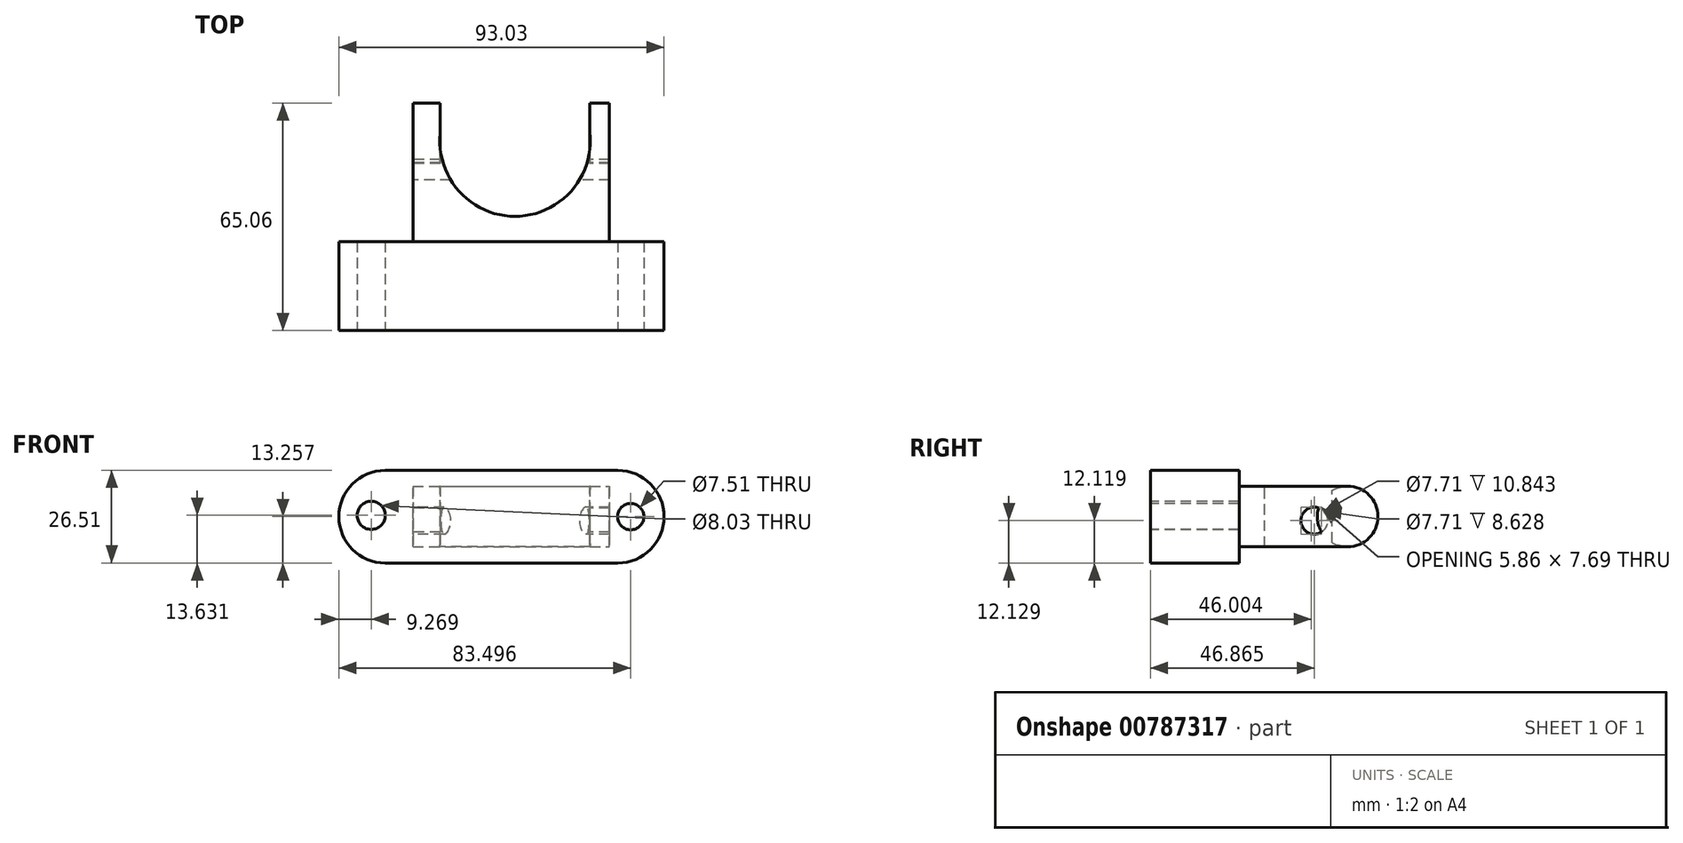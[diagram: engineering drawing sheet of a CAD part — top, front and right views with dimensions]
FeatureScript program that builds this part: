
annotation { "Feature Type Name" : "Feature", "Feature Type Description" : "" }
export const myFeature = defineFeature(function(context is Context, id is Id, definition is map)
    precondition{}
    {
        {
            var Q0;
            Q0=qCreatedBy(makeId("Front.planeOp"),FACE);
            var sketch = newSketch(context, id + "F0", { "sketchPlane" : qUnion([Q0])});
            skLineSegment(sketch, "E0.bottom", {"start": v(22.53, 17.47) * mm, "end": v(-43.98, 17.47) * mm});
            skLineSegment(sketch, "E0.top", {"start": v(22.53, -9.04) * mm, "end": v(-43.98, -9.04) * mm});
            skLineSegment(sketch, "E0.left", {"start": v(22.53, 17.47) * mm, "end": v(22.53, -9.04) * mm});
            skLineSegment(sketch, "E0.right", {"start": v(-43.98, 17.47) * mm, "end": v(-43.98, -9.04) * mm});
            skArc(sketch, "E1", {"start": v(-43.98, 17.47) * mm, "mid": v(-57.24, 4.22) * mm, "end": v(-43.98, -9.04) * mm});
            skArc(sketch, "E2", {"start": v(22.53, -9.04) * mm, "mid": v(35.79, 4.22) * mm, "end": v(22.53, 17.47) * mm});
            skSolve(sketch);
        }
        {
            var Q0;
            Q0=makeQuery(id+"F0.imprint","IMPRINT",FACE,{"disambiguationData":[TD([[makeQuery(id+"F0.imprint","IMPRINT",EDGE,{"derivedFrom":sQuery(id+"F0.wireOp",EDGE,"E0.left")}),1.0]])]});
            var Q1;
            Q1=makeQuery(id+"F0.imprint","IMPRINT",FACE,{"disambiguationData":[TD([[makeQuery(id+"F0.imprint","IMPRINT",EDGE,{"derivedFrom":sQuery(id+"F0.wireOp",EDGE,"E0.right")}),-1.0]])]});
            var Q2;
            Q2=makeQuery(id+"F0.imprint","IMPRINT",FACE,{"disambiguationData":[TD([[makeQuery(id+"F0.imprint","IMPRINT",EDGE,{"derivedFrom":sQuery(id+"F0.wireOp",EDGE,"E0.bottom")}),1.0]])]});
            extrude(context, id + "F1", {"entities" : qUnion([Q0, Q1, Q2]), "depth" : 25.4 * mm, "offsetDistance" : 25.4 * mm});
        }
        {
            var Q0;
            Q0=makeQuery(id+"F1.opExtrude","CAP_FACE",FACE,{"disambiguationData":[OSD([sQuery(id+"F0.wireOp",EDGE,"E0.bottom"),sQuery(id+"F0.wireOp",EDGE,"E0.top"),sQuery(id+"F0.wireOp",EDGE,"E1"),sQuery(id+"F0.wireOp",EDGE,"E2")])],"isStart":false});
            var sketch = newSketch(context, id + "F2", { "sketchPlane" : qUnion([Q0])});
            skCircle(sketch, "E3", {"center": v(-47.97, 4.6) * mm, "radius": 4.01 * mm});
            skCircle(sketch, "E4", {"center": v(26.26, 4.22) * mm, "radius": 3.76 * mm});
            skPoint(sketch, "E4.centerSnap0", {"position": v(35.79, 4.22) * mm});
            skSolve(sketch);
        }
        {
            var Q0;
            Q0=makeQuery(id+"F2.imprint","IMPRINT",FACE,{"disambiguationData":[TD([[makeQuery(id+"F2.imprint","IMPRINT",EDGE,{"derivedFrom":sQuery(id+"F2.wireOp",EDGE,"E3")}),1.0]])]});
            var Q1;
            Q1=makeQuery(id+"F2.imprint","IMPRINT",FACE,{"disambiguationData":[TD([[makeQuery(id+"F2.imprint","IMPRINT",EDGE,{"derivedFrom":sQuery(id+"F2.wireOp",EDGE,"E4")}),1.0]])]});
            extrude(context, id + "F3", {"entities" : qUnion([Q0, Q1]), "operationType" : NewBodyOperationType.REMOVE, "oppositeDirection" : true, "depth" : 25.4 * mm, "offsetDistance" : 25.4 * mm});
        }
        {
            var Q0;
            Q0=makeQuery(id+"F1.opExtrude","CAP_FACE",FACE,{"disambiguationData":[OSD([sQuery(id+"F0.wireOp",EDGE,"E0.bottom"),sQuery(id+"F0.wireOp",EDGE,"E0.top"),sQuery(id+"F0.wireOp",EDGE,"E1"),sQuery(id+"F0.wireOp",EDGE,"E2")])],"isStart":true});
            var sketch = newSketch(context, id + "F4", { "sketchPlane" : qUnion([Q0])});
            skLineSegment(sketch, "E5.bottom", {"start": v(36.06, -4.4) * mm, "end": v(-20.17, -4.4) * mm});
            skLineSegment(sketch, "E5.top", {"start": v(36.06, 12.94) * mm, "end": v(-20.17, 12.94) * mm});
            skLineSegment(sketch, "E5.left", {"start": v(36.06, -4.4) * mm, "end": v(36.06, 12.94) * mm});
            skLineSegment(sketch, "E5.right", {"start": v(-20.17, -4.4) * mm, "end": v(-20.17, 12.94) * mm});
            skSolve(sketch);
        }
        {
            var Q0;
            Q0=makeQuery(id+"F4.imprint","IMPRINT",FACE,{"disambiguationData":[TD([[makeQuery(id+"F4.imprint","IMPRINT",EDGE,{"derivedFrom":sQuery(id+"F4.wireOp",EDGE,"E5.bottom")}),-1.0]])]});
            extrude(context, id + "F5", {"entities" : qUnion([Q0]), "operationType" : NewBodyOperationType.ADD, "depth" : 30.99 * mm, "offsetDistance" : 25.4 * mm});
        }
        {
            var Q0;
            Q0=makeQuery(id+"F5.opExtrude","SWEPT_FACE",FACE,{"disambiguationData":[OSD([sQuery(id+"F4.wireOp",EDGE,"E5.top")])]});
            var sketch = newSketch(context, id + "F6", { "sketchPlane" : qUnion([Q0])});
            skArc(sketch, "E6", {"start": v(-28.22, 30.99) * mm, "mid": v(-6.84, 7.26) * mm, "end": v(14.55, 30.99) * mm});
            skSolve(sketch);
        }
        {
            var Q0;
            {var subQ0=sQuery(id+"F6.wireOp",EDGE,"E6");Q0=makeQuery(id+"F6.imprint","IMPRINT",FACE,{"disambiguationData":[TD([[makeQuery(id+"F6.imprint","IMPRINT",EDGE,{"derivedFrom":subQ0}),1.0]])]});}
            extrude(context, id + "F7", {"entities" : qUnion([Q0]), "operationType" : NewBodyOperationType.REMOVE, "oppositeDirection" : true, "depth" : 32.5 * mm, "offsetDistance" : 25.4 * mm});
        }
        {
            var Q0;
            Q0=makeQuery(id+"F5.opExtrude","SWEPT_FACE",FACE,{"disambiguationData":[OSD([sQuery(id+"F4.wireOp",EDGE,"E5.left")])]});
            var sketch = newSketch(context, id + "F8", { "sketchPlane" : qUnion([Q0])});
            skCircle(sketch, "E7", {"center": v(-21.47, 3.08) * mm, "radius": 3.86 * mm});
            skSolve(sketch);
        }
        {
            var Q0;
            Q0=makeQuery(id+"F8.imprint","IMPRINT",FACE,{"disambiguationData":[TD([[makeQuery(id+"F8.imprint","IMPRINT",EDGE,{"derivedFrom":sQuery(id+"F8.wireOp",EDGE,"E7")}),1.0]])]});
            extrude(context, id + "F9", {"entities" : qUnion([Q0]), "operationType" : NewBodyOperationType.REMOVE, "oppositeDirection" : true, "depth" : 79.5 * mm, "offsetDistance" : 25.4 * mm});
        }
        {
            var Q0;
            {var subQ0=sQuery(id+"F4.wireOp",EDGE,"E5.bottom");var subQ1=sQuery(id+"F4.wireOp",EDGE,"E5.top");var subQ2=sQuery(id+"F4.wireOp",EDGE,"E5.left");Q0=makeQuery(id+"F7.boolean.opBoolean","SPLIT",FACE,{"disambiguationData":[TD([makeQuery(id+"F5.opExtrude","SWEPT_FACE",FACE,{"disambiguationData":[OSD([subQ2])]})])],"derivedFrom":makeQuery(id+"F5.opExtrude","CAP_FACE",FACE,{"disambiguationData":[OSD([subQ0,subQ1,subQ2,sQuery(id+"F4.wireOp",EDGE,"E5.right")])],"isStart":false})});}
            var sketch = newSketch(context, id + "F10", { "sketchPlane" : qUnion([Q0])});
            skLineSegment(sketch, "E8", {"start": v(36.06, 4.27) * mm, "end": v(28.22, 4.27) * mm});
            skSolve(sketch);
        }
        {
            var Q0;
            {var subQ0=sQuery(id+"F4.wireOp",EDGE,"E5.bottom");var subQ1=sQuery(id+"F4.wireOp",EDGE,"E5.right");var subQ2=sQuery(id+"F4.wireOp",EDGE,"E5.top");Q0=makeQuery(id+"F7.boolean.opBoolean","SPLIT",FACE,{"disambiguationData":[TD([makeQuery(id+"F5.opExtrude","SWEPT_FACE",FACE,{"disambiguationData":[OSD([subQ1])]})])],"derivedFrom":makeQuery(id+"F5.opExtrude","CAP_FACE",FACE,{"disambiguationData":[OSD([subQ0,subQ2,sQuery(id+"F4.wireOp",EDGE,"E5.left"),subQ1])],"isStart":false})});}
            var sketch = newSketch(context, id + "F11", { "sketchPlane" : qUnion([Q0])});
            skLineSegment(sketch, "E9", {"start": v(-14.55, 4.27) * mm, "end": v(-20.17, 4.27) * mm});
            skSolve(sketch);
        }
        {
            var Q0;
            Q0 = qSketchRegion(id + "F11", true);
            var Q1;
            {var subQ0=sQuery(id+"F10.wireOp",EDGE,"E8");Q1=makeQuery(id+"F10.imprint","IMPRINT",FACE,{"disambiguationData":[TD([[makeQuery(id+"F10.imprint","IMPRINT",EDGE,{"derivedFrom":subQ0}),-1.0]])]});}
            var Q2;
            Q2=sQuery(id+"F10.wireOp",EDGE,"E8");
            revolve(context, id + "F12", {"operationType" : NewBodyOperationType.ADD, "surfaceOperationType" : NewSurfaceOperationType.NEW, "entities" : qUnion([Q0, Q1]), "axis" : qUnion([Q2]), "revolveType" : RevolveType.FULL});
        }
        {
            var Q0;
            {var subQ0=sQuery(id+"F11.wireOp",EDGE,"E9");Q0=makeQuery(id+"F11.imprint","IMPRINT",FACE,{"disambiguationData":[TD([[makeQuery(id+"F11.imprint","IMPRINT",EDGE,{"derivedFrom":subQ0}),-1.0]])]});}
            var Q1;
            Q1=sQuery(id+"F11.wireOp",EDGE,"E9");
            revolve(context, id + "F13", {"operationType" : NewBodyOperationType.ADD, "surfaceOperationType" : NewSurfaceOperationType.NEW, "entities" : qUnion([Q0]), "axis" : qUnion([Q1]), "revolveType" : RevolveType.FULL});
        }
    });
